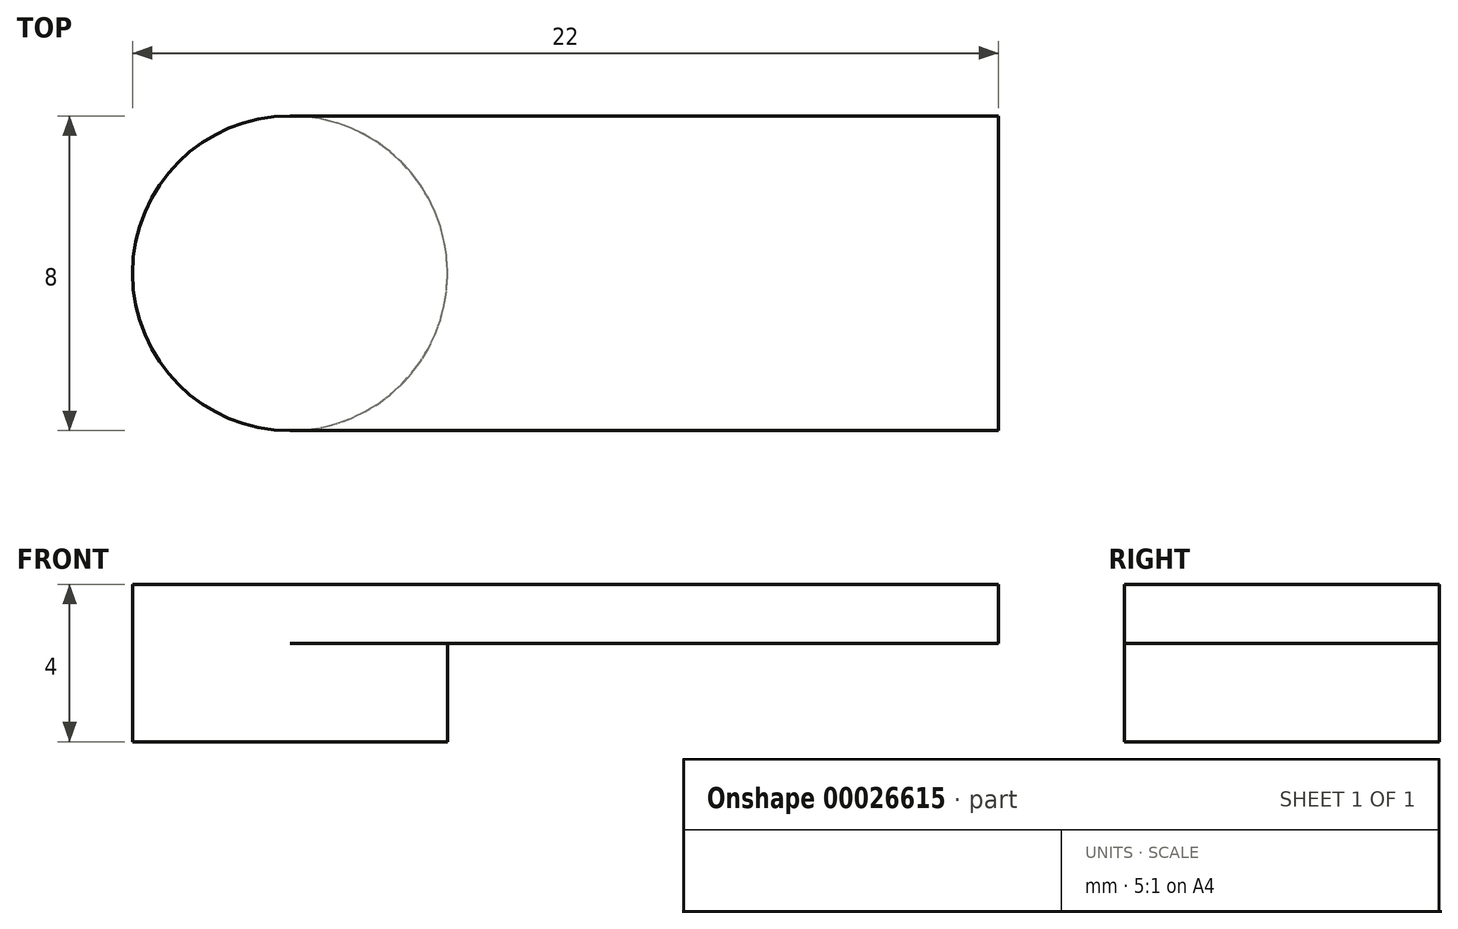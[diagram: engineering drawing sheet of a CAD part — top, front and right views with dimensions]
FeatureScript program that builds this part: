
annotation { "Feature Type Name" : "Feature", "Feature Type Description" : "" }
export const myFeature = defineFeature(function(context is Context, id is Id, definition is map)
    precondition{}
    {
        {
            var Q0;
            Q0=qCreatedBy(makeId("Top.planeOp"),FACE);
            var sketch = newSketch(context, id + "F0", { "sketchPlane" : qUnion([Q0])});
            skLineSegment(sketch, "E0.bottom", {"start": v(4, 0) * mm, "end": v(22, 0) * mm});
            skLineSegment(sketch, "E0.top", {"start": v(4, -8) * mm, "end": v(22, -8) * mm});
            skLineSegment(sketch, "E0.right", {"start": v(22, 0) * mm, "end": v(22, -8) * mm});
            skCircle(sketch, "E1", {"center": v(4, -4) * mm, "radius": 4 * mm});
            skPoint(sketch, "E2.orphan", {"position": v(0, 0) * mm});
            skSolve(sketch);
        }
        {
            var Q0;
            Q0 = qSketchRegion(id + "F0", true);
            extrude(context, id + "F1", {"entities" : qUnion([Q0]), "depth" : 1.5 * mm});
        }
        {
            var Q0;
            Q0=makeQuery(id+"F1.opExtrude","CAP_FACE",FACE,{"disambiguationData":[OSD([sQuery(id+"F0.wireOp",EDGE,"E0.bottom"),sQuery(id+"F0.wireOp",EDGE,"E0.top"),sQuery(id+"F0.wireOp",EDGE,"E0.right"),sQuery(id+"F0.wireOp",EDGE,"E1")])],"isStart":true});
            var sketch = newSketch(context, id + "F2", { "sketchPlane" : qUnion([Q0])});
            skLineSegment(sketch, "E3", {"start": v(22, 4) * mm, "end": v(0, 4) * mm, "construction": true});
            skCircle(sketch, "E4", {"center": v(4, 4) * mm, "radius": 4 * mm});
            skSolve(sketch);
        }
        {
            var Q0;
            Q0 = qSketchRegion(id + "F2", true);
            extrude(context, id + "F3", {"entities" : qUnion([Q0]), "operationType" : NewBodyOperationType.ADD, "depth" : 2.5 * mm});
        }
    });
